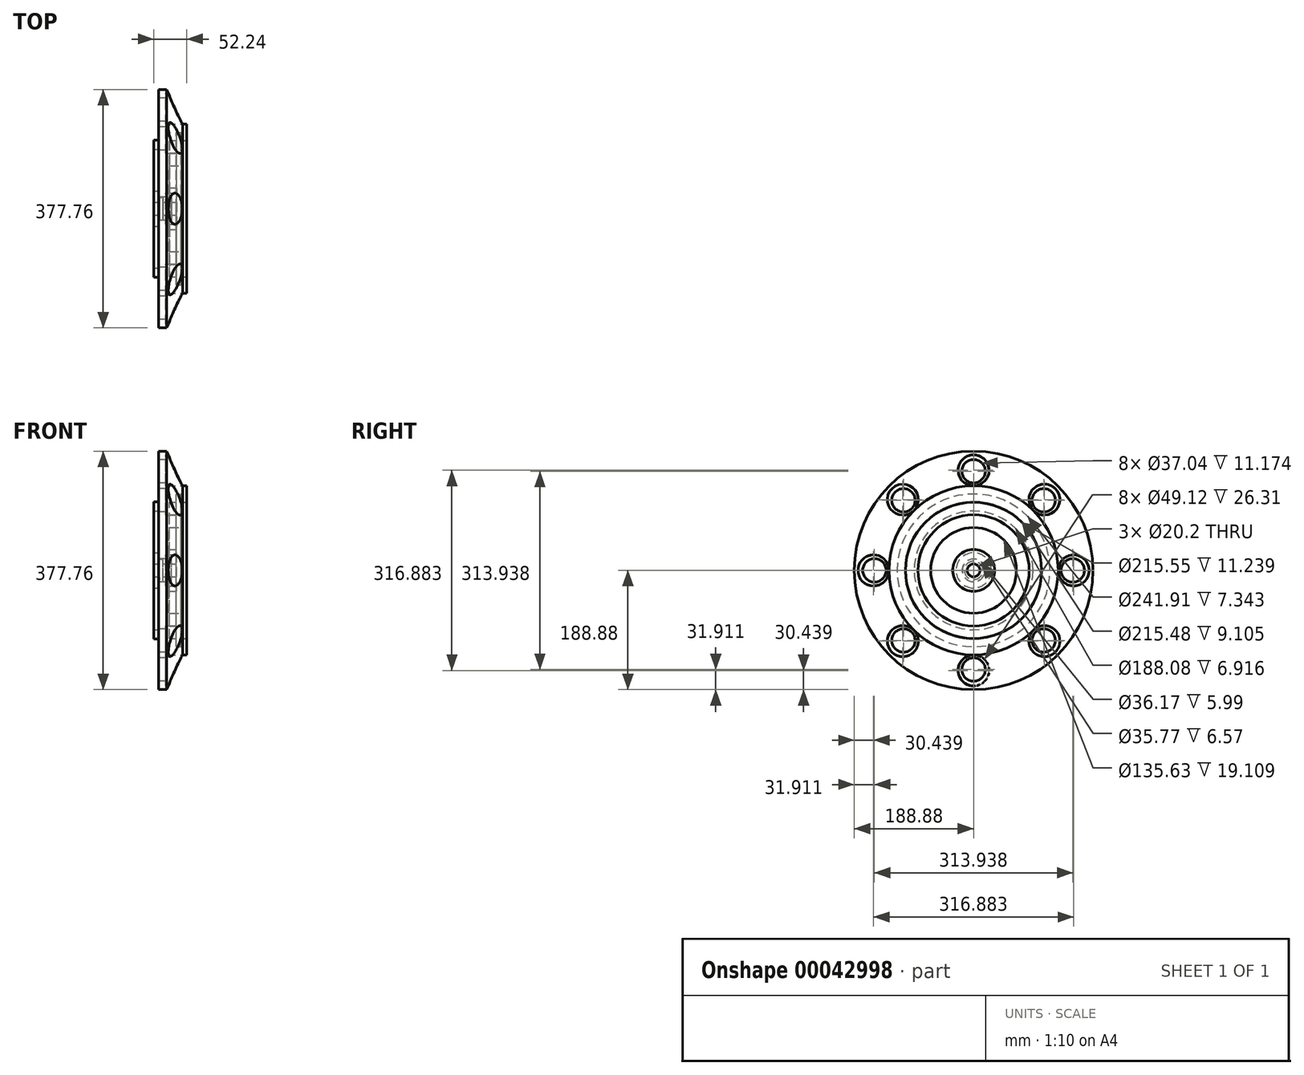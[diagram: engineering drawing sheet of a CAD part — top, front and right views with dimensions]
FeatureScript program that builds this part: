
annotation { "Feature Type Name" : "Feature", "Feature Type Description" : "" }
export const myFeature = defineFeature(function(context is Context, id is Id, definition is map)
    precondition{}
    {
        {
            var Q0;
            Q0=qCreatedBy(makeId("Front.planeOp"),FACE);
            var sketch = newSketch(context, id + "F0", { "sketchPlane" : qUnion([Q0])});
            skLineSegment(sketch, "E0", {"start": v(-31.63, 18.08) * mm, "end": v(-31.63, 14.56) * mm});
            skLineSegment(sketch, "E1", {"start": v(-23.9, 14.56) * mm, "end": v(-23.9, 18.08) * mm});
            skLineSegment(sketch, "E2", {"start": v(-23.9, 18.08) * mm, "end": v(-17.92, 18.08) * mm});
            skLineSegment(sketch, "E3", {"start": v(-17.92, 18.08) * mm, "end": v(-17.92, 14.37) * mm});
            skLineSegment(sketch, "E4", {"start": v(-11.15, 14.37) * mm, "end": v(-11.15, 17.89) * mm});
            skLineSegment(sketch, "E5", {"start": v(-11.15, 17.89) * mm, "end": v(-4.58, 17.89) * mm});
            skLineSegment(sketch, "E6", {"start": v(-4.58, 17.89) * mm, "end": v(-4.58, 13.4) * mm});
            skLineSegment(sketch, "E7", {"start": v(3.92, 12.28) * mm, "end": v(3.92, 33.15) * mm});
            skLineSegment(sketch, "E8", {"start": v(3.92, 33.15) * mm, "end": v(-8.25, 33.15) * mm});
            skLineSegment(sketch, "E9", {"start": v(-8.25, 33.15) * mm, "end": v(-8.25, 67.81) * mm});
            skLineSegment(sketch, "E10", {"start": v(-8.25, 67.81) * mm, "end": v(10.85, 67.81) * mm});
            skLineSegment(sketch, "E11", {"start": v(10.85, 67.81) * mm, "end": v(10.85, 88.02) * mm});
            skLineSegment(sketch, "E12", {"start": v(10.85, 88.02) * mm, "end": v(-7.92, 88.02) * mm});
            skLineSegment(sketch, "E13", {"start": v(-7.92, 88.02) * mm, "end": v(-7.92, 107.77) * mm});
            skLineSegment(sketch, "E14", {"start": v(-7.92, 107.77) * mm, "end": v(3.32, 107.77) * mm});
            skLineSegment(sketch, "E15", {"start": v(3.32, 107.77) * mm, "end": v(3.32, 120.96) * mm});
            skLineSegment(sketch, "E16", {"start": v(3.32, 120.96) * mm, "end": v(10.66, 120.96) * mm});
            skLineSegment(sketch, "E17", {"start": v(10.66, 120.96) * mm, "end": v(10.66, 107.74) * mm});
            skLineSegment(sketch, "E18", {"start": v(10.66, 107.74) * mm, "end": v(19.77, 107.74) * mm});
            skLineSegment(sketch, "E19", {"start": v(19.77, 107.74) * mm, "end": v(19.77, 133.88) * mm});
            skLineSegment(sketch, "E20", {"start": v(19.77, 133.88) * mm, "end": v(12.91, 133.88) * mm});
            skLineSegment(sketch, "E21", {"start": v(12.91, 133.88) * mm, "end": v(-12.22, 188.88) * mm});
            skLineSegment(sketch, "E22", {"start": v(-12.22, 188.88) * mm, "end": v(-24.57, 188.88) * mm});
            skLineSegment(sketch, "E23", {"start": v(-24.57, 188.88) * mm, "end": v(-24.57, 108.86) * mm});
            skLineSegment(sketch, "E24", {"start": v(-24.57, 108.86) * mm, "end": v(-32.47, 108.37) * mm});
            skLineSegment(sketch, "E25", {"start": v(-32.47, 108.37) * mm, "end": v(-32.47, 94.04) * mm});
            skLineSegment(sketch, "E26", {"start": v(-32.47, 94.04) * mm, "end": v(-25.56, 94.04) * mm});
            skLineSegment(sketch, "E27", {"start": v(-25.56, 94.04) * mm, "end": v(-25.56, 27.85) * mm});
            skLineSegment(sketch, "E28", {"start": v(-25.56, 27.85) * mm, "end": v(-30.52, 27.85) * mm});
            skLineSegment(sketch, "E29", {"start": v(-31.63, 18.08) * mm, "end": v(-31.63, 26.73) * mm});
            skPoint(sketch, "E30.orphan", {"position": v(-32.97, 27.85) * mm});
            skPoint(sketch, "E31.visualSharp", {"position": v(-17.92, 13.25) * mm});
            skPoint(sketch, "E32.visualSharp", {"position": v(-11.15, 13.25) * mm});
            skPoint(sketch, "E33.visualSharp", {"position": v(-23.9, 13.45) * mm});
            skPoint(sketch, "E34.visualSharp", {"position": v(-31.63, 13.45) * mm});
            skPoint(sketch, "E35.visualSharp", {"position": v(-4.58, 12.28) * mm});
            skPoint(sketch, "E36.visualSharp", {"position": v(-31.63, 27.85) * mm});
            skArc(sketch, "E36.filletArc", {"start": v(-30.52, 27.85) * mm, "mid": v(-31.3, 27.52) * mm, "end": v(-31.63, 26.73) * mm});
            skLineSegment(sketch, "E37", {"start": v(35.76, 0) * mm, "end": v(-145.13, 0) * mm, "construction": true});
            skLineSegment(sketch, "E38", {"start": v(-31.63, 14.56) * mm, "end": v(-31.63, 11.21) * mm});
            skLineSegment(sketch, "E39", {"start": v(-30.52, 10.1) * mm, "end": v(-24.95, 10.1) * mm});
            skLineSegment(sketch, "E40", {"start": v(-23.84, 11.24) * mm, "end": v(-23.9, 14.56) * mm});
            skLineSegment(sketch, "E41", {"start": v(-17.92, 14.37) * mm, "end": v(-17.92, 11.21) * mm});
            skLineSegment(sketch, "E42", {"start": v(-16.8, 10.1) * mm, "end": v(-12.27, 10.1) * mm});
            skLineSegment(sketch, "E43", {"start": v(-11.15, 11.21) * mm, "end": v(-11.15, 14.37) * mm});
            skLineSegment(sketch, "E44", {"start": v(-4.58, 13.4) * mm, "end": v(-4.58, 11.21) * mm});
            skLineSegment(sketch, "E45", {"start": v(-3.47, 10.1) * mm, "end": v(3.92, 10.1) * mm});
            skLineSegment(sketch, "E46", {"start": v(3.92, 10.1) * mm, "end": v(3.92, 12.28) * mm});
            skPoint(sketch, "E47.visualSharp", {"position": v(-31.63, 10.1) * mm});
            skArc(sketch, "E47.filletArc", {"start": v(-31.63, 11.21) * mm, "mid": v(-31.3, 10.43) * mm, "end": v(-30.52, 10.1) * mm});
            skPoint(sketch, "E48.visualSharp", {"position": v(-23.81, 10.1) * mm});
            skArc(sketch, "E48.filletArc", {"start": v(-24.95, 10.1) * mm, "mid": v(-24.16, 10.43) * mm, "end": v(-23.84, 11.24) * mm});
            skPoint(sketch, "E49.visualSharp", {"position": v(-17.92, 10.1) * mm});
            skArc(sketch, "E49.filletArc", {"start": v(-17.92, 11.21) * mm, "mid": v(-17.59, 10.43) * mm, "end": v(-16.8, 10.1) * mm});
            skPoint(sketch, "E50.visualSharp", {"position": v(-11.15, 10.1) * mm});
            skArc(sketch, "E50.filletArc", {"start": v(-12.27, 10.1) * mm, "mid": v(-11.48, 10.43) * mm, "end": v(-11.15, 11.21) * mm});
            skPoint(sketch, "E51.visualSharp", {"position": v(-4.58, 10.1) * mm});
            skArc(sketch, "E51.filletArc", {"start": v(-4.58, 11.21) * mm, "mid": v(-4.26, 10.43) * mm, "end": v(-3.47, 10.1) * mm});
            skSolve(sketch);
        }
        {
            var Q0;
            Q0=makeQuery(id+"F0.imprint","IMPRINT",FACE,{"disambiguationData":[TD([[makeQuery(id+"F0.imprint","IMPRINT",EDGE,{"derivedFrom":sQuery(id+"F0.wireOp",EDGE,"E0")}),1.0]])]});
            var Q1;
            Q1=sQuery(id+"F0.wireOp",EDGE,"E37");
            revolve(context, id + "F1", {"entities" : qUnion([Q0]), "axis" : qUnion([Q1]), "revolveType" : RevolveType.FULL});
        }
        {
            var Q0;
            Q0=makeQuery(id+"F1.opRevolve","SWEPT_FACE",FACE,{"disambiguationData":[OSD([sQuery(id+"F0.wireOp",EDGE,"E23")])]});
            var sketch = newSketch(context, id + "F2", { "sketchPlane" : qUnion([Q0])});
            skCircle(sketch, "E52", {"center": v(0, 0) * mm, "radius": 156.97 * mm, "construction": true});
            skCircle(sketch, "E53", {"center": v(0, 156.97) * mm, "radius": 18.52 * mm});
            skCircle(sketch, "E54.1.0", {"center": v(-111, 111) * mm, "radius": 18.52 * mm});
            skCircle(sketch, "E54.2.0", {"center": v(-156.97, 0) * mm, "radius": 18.52 * mm});
            skCircle(sketch, "E54.3.0", {"center": v(-111, -111) * mm, "radius": 18.52 * mm});
            skCircle(sketch, "E54.4.0", {"center": v(0, -156.97) * mm, "radius": 18.52 * mm});
            skCircle(sketch, "E54.5.0", {"center": v(111, -111) * mm, "radius": 18.52 * mm});
            skCircle(sketch, "E54.6.0", {"center": v(156.97, 0) * mm, "radius": 18.52 * mm});
            skCircle(sketch, "E54.7.0", {"center": v(111, 111) * mm, "radius": 18.52 * mm});
            skSolve(sketch);
        }
        {
            var Q0;
            Q0 = qSketchRegion(id + "F2", true);
            extrude(context, id + "F3", {"entities" : qUnion([Q0]), "operationType" : NewBodyOperationType.REMOVE, "oppositeDirection" : true, "depth" : 55.68 * mm});
        }
        {
            var Q0;
            Q0=makeQuery(id+"F1.opRevolve","SWEPT_FACE",FACE,{"disambiguationData":[OSD([sQuery(id+"F0.wireOp",EDGE,"E19")])]});
            var sketch = newSketch(context, id + "F4", { "sketchPlane" : qUnion([Q0])});
            skLineSegment(sketch, "E55", {"start": v(0, 0) * mm, "end": v(0, 189.46) * mm, "construction": true});
            skCircle(sketch, "E56", {"center": v(0, 0) * mm, "radius": 158.44 * mm, "construction": true});
            skCircle(sketch, "E57", {"center": v(0, 158.44) * mm, "radius": 24.56 * mm});
            skCircle(sketch, "E58.1.0", {"center": v(-112.03, 112.03) * mm, "radius": 24.56 * mm});
            skCircle(sketch, "E58.2.0", {"center": v(-158.44, 0) * mm, "radius": 24.56 * mm});
            skCircle(sketch, "E58.3.0", {"center": v(-112.03, -112.03) * mm, "radius": 24.56 * mm});
            skCircle(sketch, "E58.4.0", {"center": v(0, -158.44) * mm, "radius": 24.56 * mm});
            skCircle(sketch, "E58.5.0", {"center": v(112.03, -112.03) * mm, "radius": 24.56 * mm});
            skCircle(sketch, "E58.6.0", {"center": v(158.44, 0) * mm, "radius": 24.56 * mm});
            skCircle(sketch, "E58.7.0", {"center": v(112.03, 112.03) * mm, "radius": 24.56 * mm});
            skSolve(sketch);
        }
        {
            var Q0;
            Q0 = qSketchRegion(id + "F4", true);
            extrude(context, id + "F5", {"entities" : qUnion([Q0]), "operationType" : NewBodyOperationType.REMOVE, "oppositeDirection" : true, "depth" : 33.17 * mm});
        }
    });
